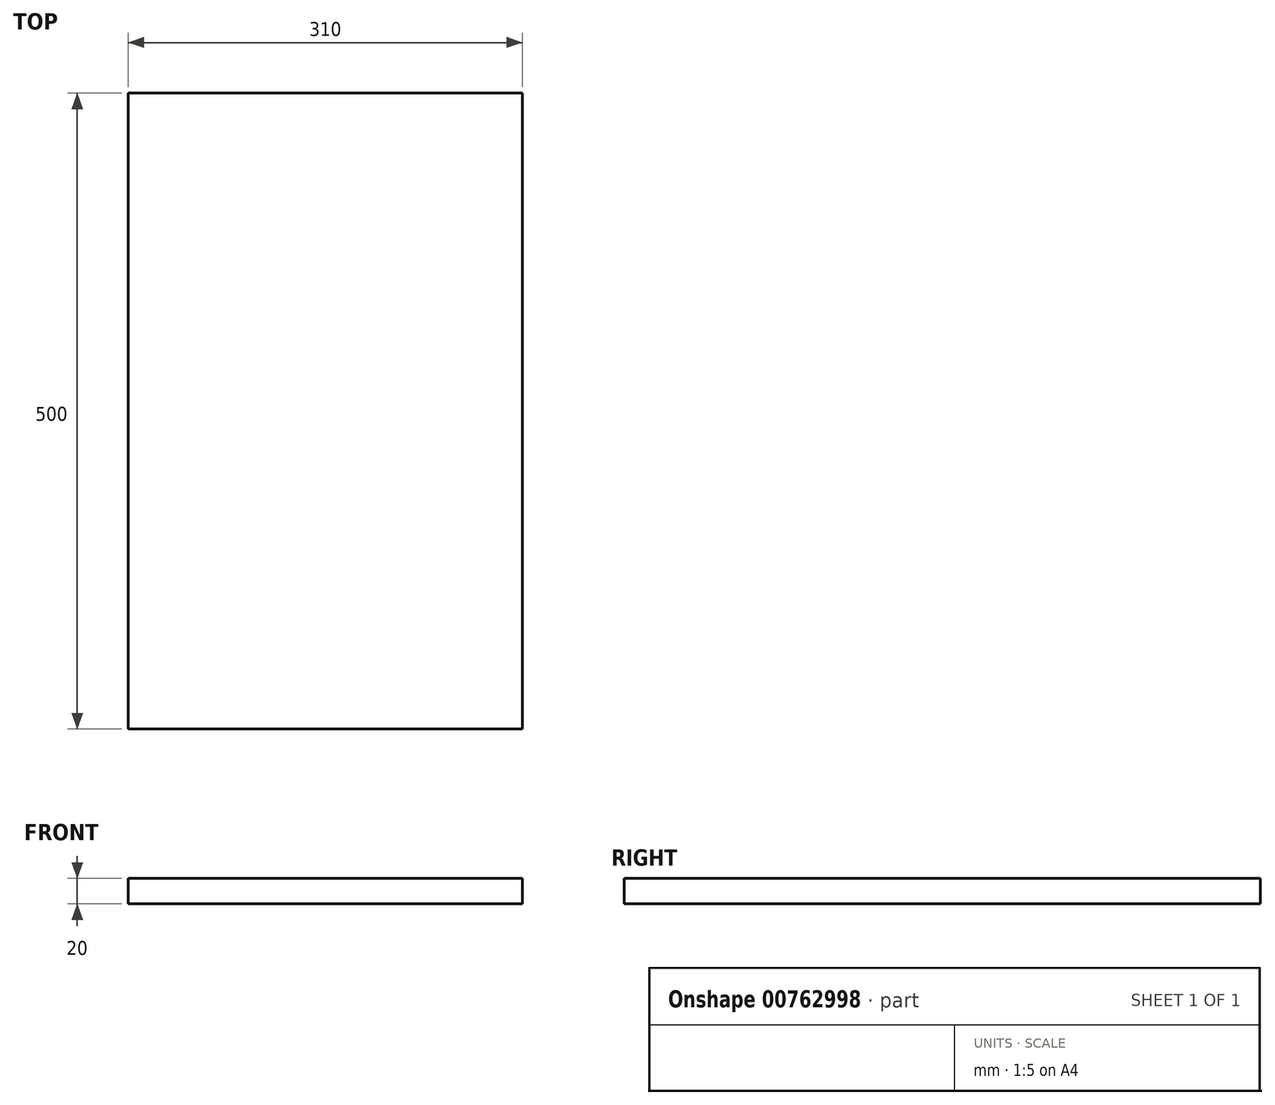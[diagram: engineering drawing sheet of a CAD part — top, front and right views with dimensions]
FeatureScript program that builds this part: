
annotation { "Feature Type Name" : "Feature", "Feature Type Description" : "" }
export const myFeature = defineFeature(function(context is Context, id is Id, definition is map)
    precondition{}
    {
        {
            var Q0;
            Q0=qCreatedBy(makeId("Top.planeOp"),FACE);
            var sketch = newSketch(context, id + "F0", { "sketchPlane" : qUnion([Q0])});
            skLineSegment(sketch, "E0.bottom", {"start": v(0, 0) * mm, "end": v(310, 0) * mm});
            skLineSegment(sketch, "E0.top", {"start": v(0, -500) * mm, "end": v(310, -500) * mm});
            skLineSegment(sketch, "E0.left", {"start": v(0, 0) * mm, "end": v(0, -500) * mm});
            skLineSegment(sketch, "E0.right", {"start": v(310, 0) * mm, "end": v(310, -500) * mm});
            skSolve(sketch);
        }
        {
            var Q0;
            Q0 = qSketchRegion(id + "F0", true);
            extrude(context, id + "F1", {"entities" : qUnion([Q0]), "oppositeDirection" : true, "depth" : 20 * mm, "offsetDistance" : 25 * mm});
        }
    });
